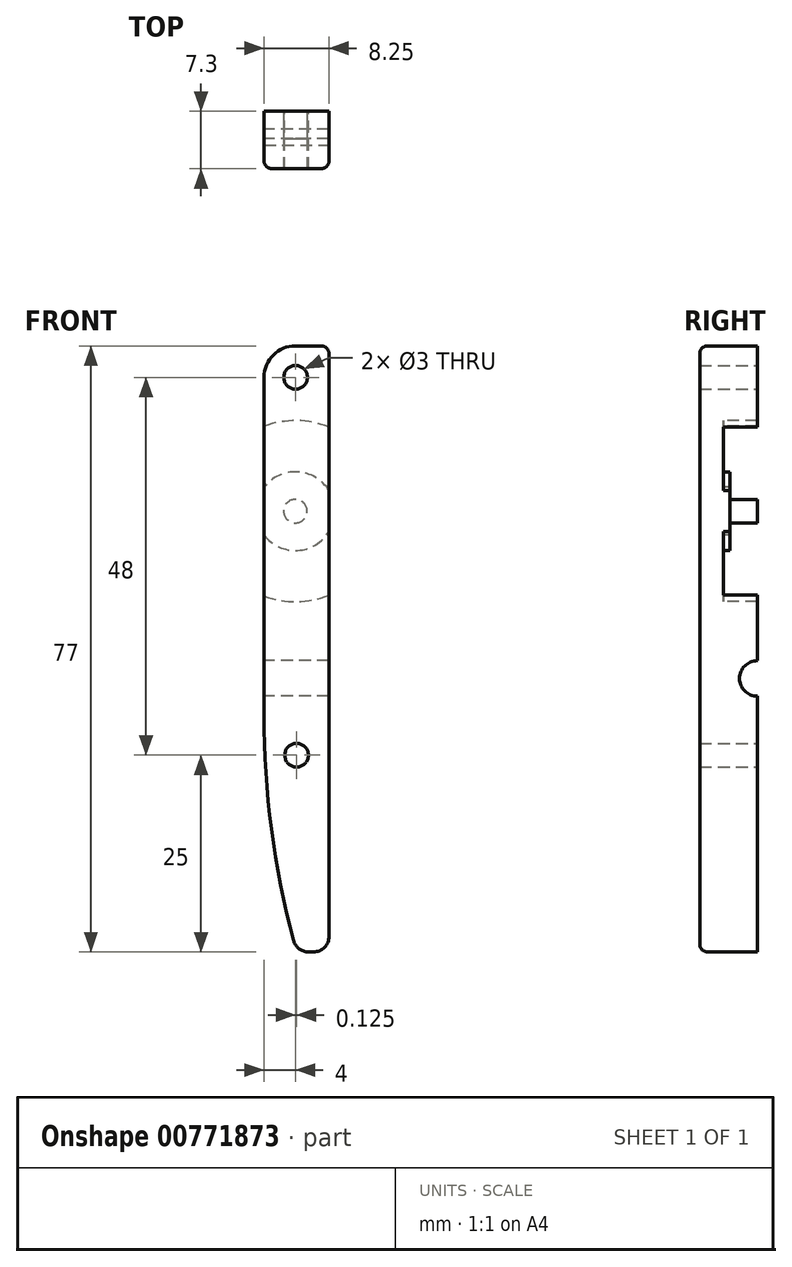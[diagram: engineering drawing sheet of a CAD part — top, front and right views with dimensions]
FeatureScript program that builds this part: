
annotation { "Feature Type Name" : "Feature", "Feature Type Description" : "" }
export const myFeature = defineFeature(function(context is Context, id is Id, definition is map)
    precondition{}
    {
        {
            var Q0;
            Q0=qCreatedBy(makeId("Front.planeOp"),FACE);
            var sketch = newSketch(context, id + "F0", { "sketchPlane" : qUnion([Q0])});
            skLineSegment(sketch, "E0.top", {"start": v(4, 47) * mm, "end": v(8.25, 47) * mm});
            skLineSegment(sketch, "E0.left", {"start": v(0, 0) * mm, "end": v(0, 43) * mm});
            skLineSegment(sketch, "E0.right", {"start": v(8.25, -28) * mm, "end": v(8.25, 47) * mm});
            skCircle(sketch, "E1", {"center": v(4, 43) * mm, "radius": 1.5 * mm});
            skPoint(sketch, "E2.visualSharp", {"position": v(0, 47) * mm});
            skArc(sketch, "E2.filletArc", {"start": v(4, 47) * mm, "mid": v(1.17, 45.83) * mm, "end": v(0, 43) * mm});
            skCircle(sketch, "E3", {"center": v(3.98, 26) * mm, "radius": 3.98 * mm});
            skArc(sketch, "E4", {"start": v(8.25, 28.6) * mm, "mid": v(4.24, 31) * mm, "end": v(0, 29.03) * mm});
            skArc(sketch, "E5.trimOffspring", {"start": v(0, 22.97) * mm, "mid": v(4.24, 21) * mm, "end": v(8.25, 23.4) * mm});
            skArc(sketch, "E6", {"start": v(0, 0) * mm, "mid": v(0.93, -14.38) * mm, "end": v(3.72, -28.51) * mm});
            skLineSegment(sketch, "E7", {"start": v(6.25, -30) * mm, "end": v(5.65, -30) * mm});
            skPoint(sketch, "E8.visualSharp", {"position": v(4.13, -30) * mm});
            skArc(sketch, "E8.filletArc", {"start": v(3.72, -28.51) * mm, "mid": v(4.43, -29.59) * mm, "end": v(5.65, -30) * mm});
            skPoint(sketch, "E9.visualSharp", {"position": v(8.25, -30) * mm});
            skArc(sketch, "E9.filletArc", {"start": v(6.25, -30) * mm, "mid": v(7.66, -29.41) * mm, "end": v(8.25, -28) * mm});
            skArc(sketch, "E10", {"start": v(8.25, 36.68) * mm, "mid": v(4.14, 37.5) * mm, "end": v(0, 36.8) * mm});
            skArc(sketch, "E11.trimOffspring", {"start": v(0, 15.2) * mm, "mid": v(4.14, 14.5) * mm, "end": v(8.25, 15.32) * mm});
            skLineSegment(sketch, "E12", {"start": v(8.25, 26) * mm, "end": v(7.95, 26) * mm});
            skCircle(sketch, "E13", {"center": v(3.98, 26) * mm, "radius": 1.5 * mm});
            skLineSegment(sketch, "E14", {"start": v(0, 0) * mm, "end": v(8.25, 0) * mm});
            skCircle(sketch, "E15", {"center": v(4.13, -5) * mm, "radius": 1.5 * mm});
            skPoint(sketch, "E16", {"position": v(4.13, 0) * mm});
            skSolve(sketch);
        }
        {
            var Q0;
            Q0=qCreatedBy(makeId("Right.planeOp"),FACE);
            var sketch = newSketch(context, id + "F1", { "sketchPlane" : qUnion([Q0])});
            skCircle(sketch, "E17", {"center": v(-4.3, 4.75) * mm, "radius": 2.25 * mm});
            skSolve(sketch);
        }
        {
            var Q0;
            Q0=qCreatedBy(makeId("Top.planeOp"),FACE);
            var sketch = newSketch(context, id + "F2", { "sketchPlane" : qUnion([Q0])});
            skArc(sketch, "E18", {"start": v(8.25, 2) * mm, "mid": v(7.96, 2.7) * mm, "end": v(7.25, 3) * mm});
            skLineSegment(sketch, "E19", {"start": v(8.25, 2) * mm, "end": v(8.25, 3) * mm});
            skLineSegment(sketch, "E20", {"start": v(8.25, 3) * mm, "end": v(7.25, 3) * mm});
            skSolve(sketch);
        }
        {
            var Q0;
            {var subQ2=sQuery(id+"F0.wireOp",EDGE,"E11.trimOffspring");Q0=makeQuery(id+"F0.imprint","IMPRINT",FACE,{"disambiguationData":[TD([[makeQuery(id+"F0.imprint","IMPRINT",EDGE,{"derivedFrom":subQ2}),-1.0]])]});}
            var Q1;
            {var subQ0=sQuery(id+"F0.wireOp",EDGE,"E5.trimOffspring");Q1=makeQuery(id+"F0.imprint","IMPRINT",FACE,{"disambiguationData":[TD([[makeQuery(id+"F0.imprint","IMPRINT",EDGE,{"derivedFrom":subQ0}),-1.0]])]});}
            var Q2;
            {var subQ0=sQuery(id+"F0.wireOp",EDGE,"E5.trimOffspring");Q2=makeQuery(id+"F0.imprint","IMPRINT",FACE,{"disambiguationData":[TD([[makeQuery(id+"F0.imprint","IMPRINT",EDGE,{"derivedFrom":subQ0}),1.0]])]});}
            var Q3;
            Q3=makeQuery(id+"F0.imprint","IMPRINT",FACE,{"disambiguationData":[TD([[makeQuery(id+"F0.imprint","IMPRINT",EDGE,{"derivedFrom":sQuery(id+"F0.wireOp",EDGE,"E13")}),-1.0]])]});
            var Q4;
            Q4=makeQuery(id+"F0.imprint","IMPRINT",FACE,{"disambiguationData":[TD([[makeQuery(id+"F0.imprint","IMPRINT",EDGE,{"derivedFrom":sQuery(id+"F0.wireOp",EDGE,"E13")}),1.0]])]});
            var Q5;
            {var subQ0=sQuery(id+"F0.wireOp",EDGE,"E4");Q5=makeQuery(id+"F0.imprint","IMPRINT",FACE,{"disambiguationData":[TD([[makeQuery(id+"F0.imprint","IMPRINT",EDGE,{"derivedFrom":subQ0}),1.0]])]});}
            var Q6;
            {var subQ0=sQuery(id+"F0.wireOp",EDGE,"E4");Q6=makeQuery(id+"F0.imprint","IMPRINT",FACE,{"disambiguationData":[TD([[makeQuery(id+"F0.imprint","IMPRINT",EDGE,{"derivedFrom":subQ0}),-1.0]])]});}
            var Q7;
            {var subQ1=sQuery(id+"F0.wireOp",EDGE,"E0.top");Q7=makeQuery(id+"F0.imprint","IMPRINT",FACE,{"disambiguationData":[TD([[makeQuery(id+"F0.imprint","IMPRINT",EDGE,{"derivedFrom":subQ1}),-1.0]])]});}
            var Q8;
            Q8=makeQuery(id+"F0.imprint","IMPRINT",FACE,{"disambiguationData":[TD([[makeQuery(id+"F0.imprint","IMPRINT",EDGE,{"derivedFrom":sQuery(id+"F0.wireOp",EDGE,"E6")}),1.0]])]});
            var Q9;
            Q9=makeQuery(id+"FAmcVWsY9k6DivJ_0.opExtrude","CAP_FACE",FACE,{"disambiguationData":[OSD([sQuery(id+"F0.wireOp",EDGE,"E0.right"),sQuery(id+"F0.wireOp",EDGE,"E6"),sQuery(id+"F0.wireOp",EDGE,"E7"),sQuery(id+"F0.wireOp",EDGE,"E8.filletArc"),sQuery(id+"F0.wireOp",EDGE,"E9.filletArc"),sQuery(id+"F0.wireOp",EDGE,"E14")])],"isStart":false});
            extrude(context, id + "F3", {"entities" : qUnion([Q0, Q1, Q2, Q3, Q4, Q5, Q6, Q7, Q8]), "oppositeDirection" : true, "depth" : 3 * mm, "endBoundEntityFace" : qUnion([Q9]), "offsetDistance" : 25 * mm});
        }
        {
            var Q0;
            {var subQ1=sQuery(id+"F0.wireOp",EDGE,"E0.top");Q0=makeQuery(id+"F0.imprint","IMPRINT",FACE,{"disambiguationData":[TD([[makeQuery(id+"F0.imprint","IMPRINT",EDGE,{"derivedFrom":subQ1}),-1.0]])]});}
            var Q1;
            {var subQ3=sQuery(id+"F0.wireOp",EDGE,"E6");Q1=makeQuery(id+"F0.imprint","IMPRINT",FACE,{"disambiguationData":[TD([[makeQuery(id+"F0.imprint","IMPRINT",EDGE,{"derivedFrom":subQ3}),1.0]])]});}
            var Q2;
            Q2=makeQuery(id+"F0.imprint","IMPRINT",FACE,{"disambiguationData":[TD([[makeQuery(id+"F0.imprint","IMPRINT",EDGE,{"derivedFrom":sQuery(id+"F0.wireOp",EDGE,"E13")}),1.0]])]});
            var Q3;
            {var subQ2=sQuery(id+"F0.wireOp",EDGE,"E11.trimOffspring");Q3=makeQuery(id+"F0.imprint","IMPRINT",FACE,{"disambiguationData":[TD([[makeQuery(id+"F0.imprint","IMPRINT",EDGE,{"derivedFrom":subQ2}),-1.0]])]});}
            extrude(context, id + "F4", {"entities" : qUnion([Q0, Q1, Q2, Q3]), "operationType" : NewBodyOperationType.ADD, "depth" : 4.3 * mm, "offsetDistance" : 25 * mm});
        }
        {
            var Q0;
            Q0=makeQuery(id+"F0.imprint","IMPRINT",FACE,{"disambiguationData":[TD([[makeQuery(id+"F0.imprint","IMPRINT",EDGE,{"derivedFrom":sQuery(id+"F0.wireOp",EDGE,"E3")}),1.0]])]});
            extrude(context, id + "F5", {"entities" : qUnion([Q0]), "operationType" : NewBodyOperationType.ADD, "depth" : 0.8 * mm, "offsetDistance" : 25 * mm});
        }
        {
            var Q0;
            {var subQ0=sQuery(id+"F0.wireOp",EDGE,"E4");Q0=makeQuery(id+"F0.imprint","IMPRINT",FACE,{"disambiguationData":[TD([[makeQuery(id+"F0.imprint","IMPRINT",EDGE,{"derivedFrom":subQ0}),1.0]])]});}
            extrude(context, id + "F6", {"entities" : qUnion([Q0]), "operationType" : NewBodyOperationType.ADD, "depth" : .8 * mm, "offsetDistance" : 25 * mm});
        }
        {
            var Q0;
            Q0=makeQuery(id+"F1.imprint","IMPRINT",FACE,{"disambiguationData":[TD([[makeQuery(id+"F1.imprint","IMPRINT",EDGE,{"derivedFrom":sQuery(id+"F1.wireOp",EDGE,"E17")}),1.0]])]});
            var Q1;
            {var subQ0=sQuery(id+"F0.wireOp",EDGE,"E0.right");Q1=makeQuery(id+"F8.boolean.opBoolean","MERGE",FACE,{"derivedFrom":[makeQuery(id+"F6.boolean.opBoolean","MERGE",FACE,{"derivedFrom":[makeQuery(id+"F4.boolean.opBoolean","MERGE",FACE,{"derivedFrom":[makeQuery(id+"FAmcVWsY9k6DivJ_0.opExtrude","SWEPT_FACE",FACE,{"disambiguationData":[OSD([subQ0])]}),makeQuery(id+"F4.opExtrude","SWEPT_FACE",FACE,{"disambiguationData":[OSD([subQ0]),TDD([makeQuery(id+"F0.imprint","IMPRINT",EDGE,{"disambiguationData":[TD([[makeQuery(id+"F0.imprint","INTERSECT",VERTEX,{"derivedFrom":[subQ0,sQuery(id+"F0.wireOp",EDGE,"E9.filletArc")]}),-1.0]])],"derivedFrom":subQ0})])]}),makeQuery(id+"F4.opExtrude","SWEPT_FACE",FACE,{"disambiguationData":[OSD([subQ0]),TDD([makeQuery(id+"F0.imprint","IMPRINT",EDGE,{"disambiguationData":[TD([[makeQuery(id+"F0.imprint","INTERSECT",VERTEX,{"derivedFrom":[sQuery(id+"F0.wireOp",EDGE,"E0.top"),subQ0]}),1.0]])],"derivedFrom":subQ0})])]})]}),makeQuery(id+"F6.opExtrude","SWEPT_FACE",FACE,{"disambiguationData":[OSD([subQ0])]})]}),makeQuery(id+"F8.opExtrude","SWEPT_FACE",FACE,{"disambiguationData":[OSD([subQ0])]})]});}
            extrude(context, id + "F7", {"entities" : qUnion([Q0]), "operationType" : NewBodyOperationType.REMOVE, "endBound" : BoundingType.UP_TO_SURFACE, "depth" : 25 * mm, "endBoundEntityFace" : qUnion([Q1]), "offsetDistance" : 25 * mm});
        }
        {
            var Q0;
            {var subQ4=sQuery(id+"F0.wireOp",EDGE,"E5.trimOffspring");Q0=makeQuery(id+"F0.imprint","IMPRINT",FACE,{"disambiguationData":[TD([[makeQuery(id+"F0.imprint","IMPRINT",EDGE,{"derivedFrom":subQ4}),1.0]])]});}
            extrude(context, id + "F8", {"entities" : qUnion([Q0]), "operationType" : NewBodyOperationType.ADD, "depth" : .8 * mm, "offsetDistance" : 25 * mm});
        }
        {
            var Q0;
            Q0=makeQuery(id+"F2.imprint","IMPRINT",FACE,{"disambiguationData":[TD([[makeQuery(id+"F2.imprint","IMPRINT",EDGE,{"derivedFrom":sQuery(id+"F2.wireOp",EDGE,"E18")}),-1.0]])]});
            var Q1;
            Q1=makeQuery(id+"F3.opExtrude","CAP_EDGE",EDGE,{"disambiguationData":[OSD([sQuery(id+"F0.wireOp",EDGE,"E0.right")])],"isStart":false});
            var Q2;
            Q2=makeQuery(id+"F3.opExtrude","CAP_EDGE",EDGE,{"disambiguationData":[OSD([sQuery(id+"F0.wireOp",EDGE,"E9.filletArc")])],"isStart":false});
            var Q3;
            Q3=makeQuery(id+"F3.opExtrude","CAP_EDGE",EDGE,{"disambiguationData":[OSD([sQuery(id+"F0.wireOp",EDGE,"E8.filletArc")])],"isStart":false});
            var Q4;
            Q4=makeQuery(id+"F3.opExtrude","CAP_EDGE",EDGE,{"disambiguationData":[OSD([sQuery(id+"F0.wireOp",EDGE,"E7")])],"isStart":false});
            var Q5;
            Q5=makeQuery(id+"F3.opExtrude","CAP_EDGE",EDGE,{"disambiguationData":[OSD([sQuery(id+"F0.wireOp",EDGE,"E6")])],"isStart":false});
            var Q6;
            Q6=makeQuery(id+"F3.opExtrude","CAP_EDGE",EDGE,{"disambiguationData":[OSD([sQuery(id+"F0.wireOp",EDGE,"E0.left")])],"isStart":false});
            var Q7;
            Q7=makeQuery(id+"F3.opExtrude","CAP_EDGE",EDGE,{"disambiguationData":[OSD([sQuery(id+"F0.wireOp",EDGE,"E2.filletArc")])],"isStart":false});
            var Q8;
            Q8=makeQuery(id+"F3.opExtrude","CAP_EDGE",EDGE,{"disambiguationData":[OSD([sQuery(id+"F0.wireOp",EDGE,"E0.top")])],"isStart":false});
            sweep(context, id + "F9", {"operationType" : NewBodyOperationType.REMOVE, "profiles" : qUnion([Q0]), "path" : qUnion([Q1, Q2, Q3, Q4, Q5, Q6, Q7, Q8])});
        }
        {
            var Q0;
            {var subQ0=sQuery(id+"F0.wireOp",EDGE,"E0.right");var subQ1=sQuery(id+"F0.wireOp",EDGE,"E0.top");Q0=makeQuery(id+"F4.boolean.opBoolean","MERGE",EDGE,{"derivedFrom":[makeQuery(id+"F3.opExtrude","SWEPT_EDGE",EDGE,{"disambiguationData":[OSD([subQ1,subQ0])]}),makeQuery(id+"F4.opExtrude","SWEPT_EDGE",EDGE,{"disambiguationData":[OSD([subQ1,subQ0])]})]});}
            fillet(context, id + "F10", {"entities" : qUnion([Q0]), "radius" : 1 * mm, "tangentPropagation" : true, "allowEdgeOverflow" : false});
        }
        {
            var Q0;
            Q0=makeQuery(id+"F3.opExtrude","SWEPT_BODY",BODY,{"disambiguationData":[OSD([sQuery(id+"F0.wireOp",EDGE,"E0.top"),sQuery(id+"F0.wireOp",EDGE,"E0.left"),sQuery(id+"F0.wireOp",EDGE,"E0.right"),sQuery(id+"F0.wireOp",EDGE,"E1"),sQuery(id+"F0.wireOp",EDGE,"E2.filletArc"),sQuery(id+"F0.wireOp",EDGE,"E6"),sQuery(id+"F0.wireOp",EDGE,"E7"),sQuery(id+"F0.wireOp",EDGE,"E8.filletArc"),sQuery(id+"F0.wireOp",EDGE,"E9.filletArc")])]});
            var Q1;
            Q1=qCreatedBy(makeId("Front.planeOp"),FACE);
            mirror(context, id + "F11", {"entities" : qUnion([Q0]), "mirrorPlane" : qUnion([Q1])});
        }
        {
            var Q0;
            Q0=makeQuery(id+"F3.opExtrude","SWEPT_BODY",BODY,{"disambiguationData":[OSD([sQuery(id+"F0.wireOp",EDGE,"E0.top"),sQuery(id+"F0.wireOp",EDGE,"E0.left"),sQuery(id+"F0.wireOp",EDGE,"E0.right"),sQuery(id+"F0.wireOp",EDGE,"E1"),sQuery(id+"F0.wireOp",EDGE,"E2.filletArc"),sQuery(id+"F0.wireOp",EDGE,"E6"),sQuery(id+"F0.wireOp",EDGE,"E7"),sQuery(id+"F0.wireOp",EDGE,"E8.filletArc"),sQuery(id+"F0.wireOp",EDGE,"E9.filletArc")])]});
            deleteBodies(context, id + "F12", {"entities" : qUnion([Q0])});
        }
    });
